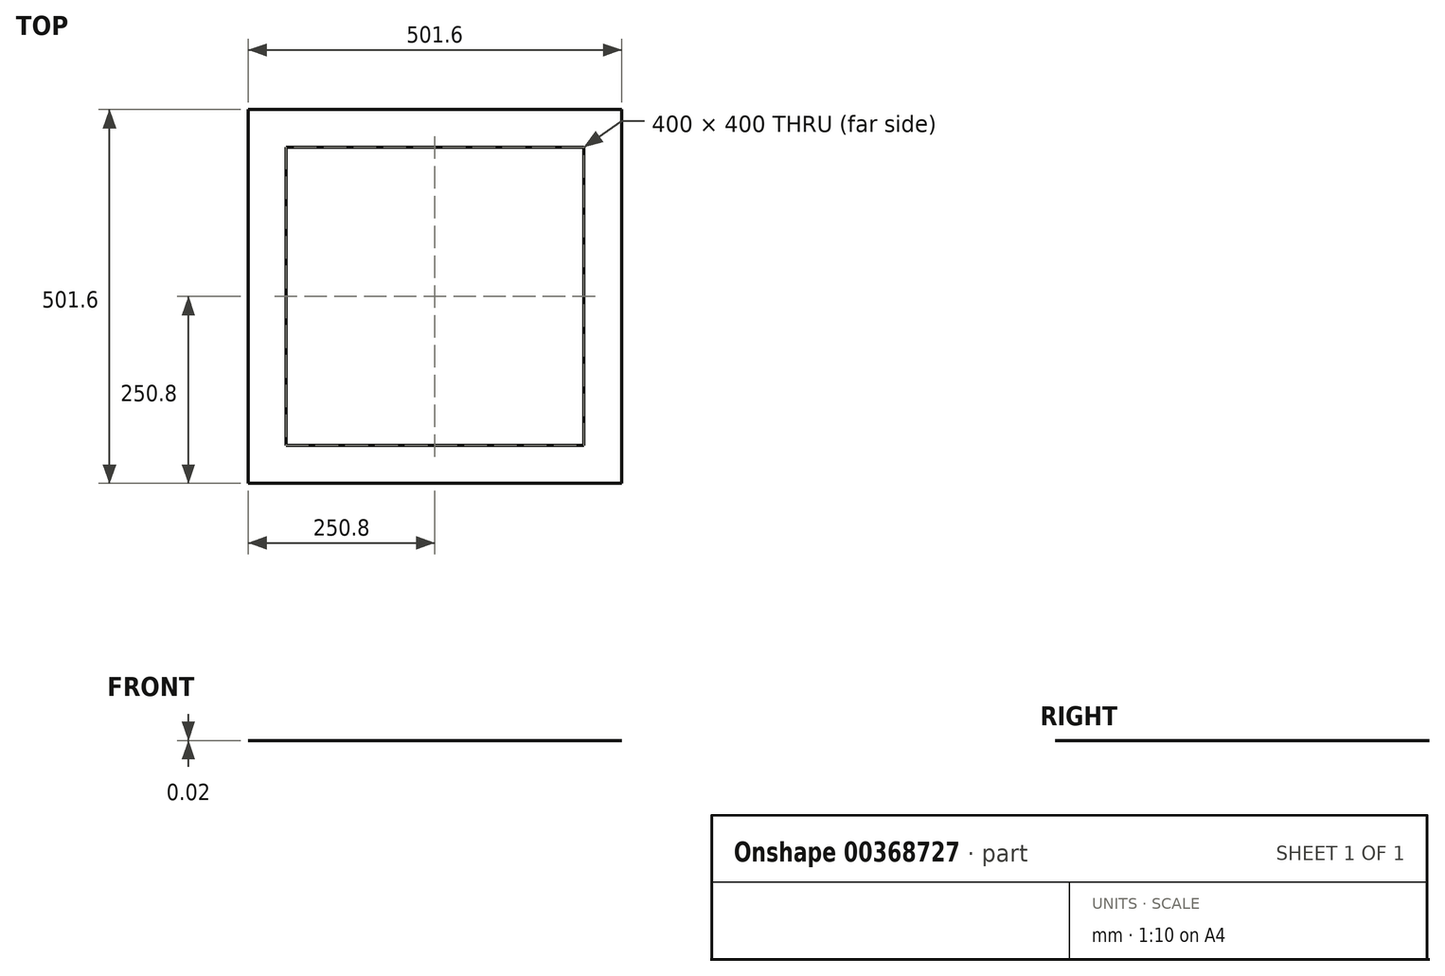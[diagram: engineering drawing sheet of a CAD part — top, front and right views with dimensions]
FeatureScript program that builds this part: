
annotation { "Feature Type Name" : "Feature", "Feature Type Description" : "" }
export const myFeature = defineFeature(function(context is Context, id is Id, definition is map)
    precondition{}
    {
        {
            var Q0;
            Q0=qCreatedBy(makeId("Top.planeOp"),FACE);
            var sketch = newSketch(context, id + "F0", { "sketchPlane" : qUnion([Q0])});
            skLineSegment(sketch, "E0.bottom", {"start": v(200, 200) * mm, "end": v(-200, 200) * mm});
            skLineSegment(sketch, "E0.top", {"start": v(200, -200) * mm, "end": v(-200, -200) * mm});
            skLineSegment(sketch, "E0.left", {"start": v(200, 200) * mm, "end": v(200, -200) * mm});
            skLineSegment(sketch, "E0.right", {"start": v(-200, 200) * mm, "end": v(-200, -200) * mm});
            skPoint(sketch, "E0.middle", {"position": v(0, 0) * mm});
            skLineSegment(sketch, "E1.bottom", {"start": v(250.8, 250.8) * mm, "end": v(-250.8, 250.8) * mm});
            skLineSegment(sketch, "E1.top", {"start": v(250.8, -250.8) * mm, "end": v(-250.8, -250.8) * mm});
            skLineSegment(sketch, "E1.left", {"start": v(250.8, 250.8) * mm, "end": v(250.8, -250.8) * mm});
            skLineSegment(sketch, "E1.right", {"start": v(-250.8, 250.8) * mm, "end": v(-250.8, -250.8) * mm});
            skSolve(sketch);
        }
        {
            var Q0;
            Q0=makeQuery(id+"F0.imprint","IMPRINT",FACE,{"disambiguationData":[TD([[makeQuery(id+"F0.imprint","IMPRINT",EDGE,{"derivedFrom":sQuery(id+"F0.wireOp",EDGE,"E0.bottom")}),-1.0]])]});
            extrude(context, id + "F1", {"entities" : qUnion([Q0]), "depth" : 1 / 50.8 * mm});
        }
    });
